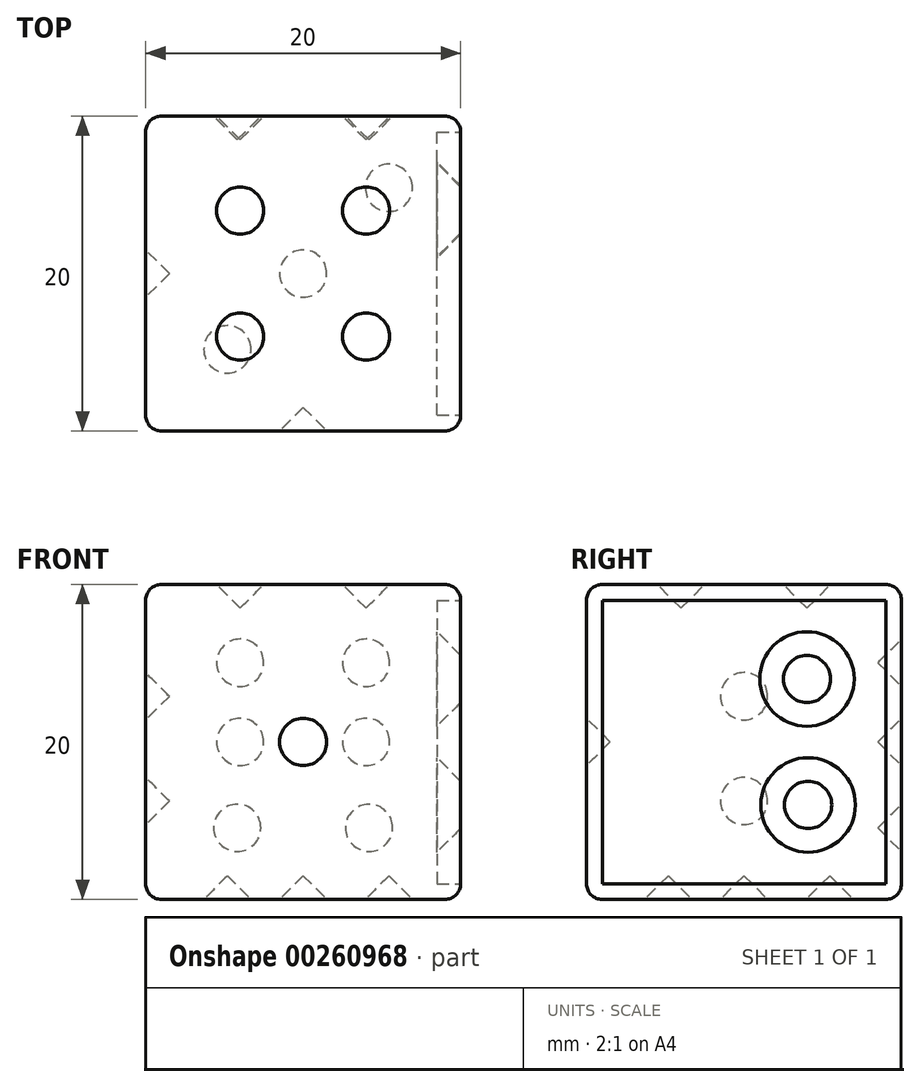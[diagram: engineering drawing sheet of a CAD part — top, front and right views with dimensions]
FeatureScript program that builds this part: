
annotation { "Feature Type Name" : "Feature", "Feature Type Description" : "" }
export const myFeature = defineFeature(function(context is Context, id is Id, definition is map)
    precondition{}
    {
        {
            var Q0;
            Q0=qCreatedBy(makeId("Top.planeOp"),FACE);
            var sketch = newSketch(context, id + "F0", { "sketchPlane" : qUnion([Q0])});
            skLineSegment(sketch, "E0.bottom", {"start": v(0, 0) * mm, "end": v(20, 0) * mm});
            skLineSegment(sketch, "E0.top", {"start": v(0, 20) * mm, "end": v(20, 20) * mm});
            skLineSegment(sketch, "E0.left", {"start": v(0, 0) * mm, "end": v(0, 20) * mm});
            skLineSegment(sketch, "E0.right", {"start": v(20, 0) * mm, "end": v(20, 20) * mm});
            skSolve(sketch);
        }
        {
            var Q0;
            Q0 = qSketchRegion(id + "F0", true);
            extrude(context, id + "F1", {"entities" : qUnion([Q0]), "depth" : 20 * mm});
        }
        {
            var Q0;
            Q0=makeQuery(id+"F1.opExtrude","SWEPT_FACE",FACE,{"disambiguationData":[OSD([sQuery(id+"F0.wireOp",EDGE,"E0.bottom")])]});
            var sketch = newSketch(context, id + "F2", { "sketchPlane" : qUnion([Q0])});
            skLineSegment(sketch, "E1.0", {"start": v(0, 20) * mm, "end": v(20, 20) * mm, "construction": true});
            skLineSegment(sketch, "E1.1", {"start": v(0, 0) * mm, "end": v(20, 0) * mm, "construction": true});
            skLineSegment(sketch, "E2", {"start": v(10, 20) * mm, "end": v(10, 0) * mm, "construction": true});
            skCircle(sketch, "E3", {"center": v(10, 10) * mm, "radius": 1.5 * mm});
            skSolve(sketch);
        }
        {
            var Q0;
            Q0 = qSketchRegion(id + "F2", true);
            extrude(context, id + "F3", {"entities" : qUnion([Q0]), "operationType" : NewBodyOperationType.REMOVE, "oppositeDirection" : true, "depth" : 1.5 * mm});
        }
        {
            var Q0;
            Q0=makeQuery(id+"F1.opExtrude","CAP_EDGE",EDGE,{"disambiguationData":[OSD([sQuery(id+"F0.wireOp",EDGE,"E0.left")])],"isStart":false});
            var Q1;
            Q1=makeQuery(id+"F1.opExtrude","CAP_EDGE",EDGE,{"disambiguationData":[OSD([sQuery(id+"F0.wireOp",EDGE,"E0.top")])],"isStart":false});
            var Q2;
            Q2=makeQuery(id+"F1.opExtrude","CAP_EDGE",EDGE,{"disambiguationData":[OSD([sQuery(id+"F0.wireOp",EDGE,"E0.right")])],"isStart":false});
            var Q3;
            Q3=makeQuery(id+"F1.opExtrude","CAP_EDGE",EDGE,{"disambiguationData":[OSD([sQuery(id+"F0.wireOp",EDGE,"E0.bottom")])],"isStart":false});
            var Q4;
            Q4=makeQuery(id+"F1.opExtrude","SWEPT_EDGE",EDGE,{"disambiguationData":[OSD([sQuery(id+"F0.wireOp",EDGE,"E0.bottom"),sQuery(id+"F0.wireOp",EDGE,"E0.right")])]});
            var Q5;
            Q5=makeQuery(id+"F1.opExtrude","CAP_EDGE",EDGE,{"disambiguationData":[OSD([sQuery(id+"F0.wireOp",EDGE,"E0.bottom")])],"isStart":true});
            var Q6;
            Q6=makeQuery(id+"F1.opExtrude","SWEPT_EDGE",EDGE,{"disambiguationData":[OSD([sQuery(id+"F0.wireOp",EDGE,"E0.bottom"),sQuery(id+"F0.wireOp",EDGE,"E0.left")])]});
            var Q7;
            Q7=makeQuery(id+"F1.opExtrude","CAP_EDGE",EDGE,{"disambiguationData":[OSD([sQuery(id+"F0.wireOp",EDGE,"E0.right")])],"isStart":true});
            var Q8;
            Q8=makeQuery(id+"F1.opExtrude","SWEPT_EDGE",EDGE,{"disambiguationData":[OSD([sQuery(id+"F0.wireOp",EDGE,"E0.top"),sQuery(id+"F0.wireOp",EDGE,"E0.right")])]});
            var Q9;
            Q9=makeQuery(id+"F1.opExtrude","CAP_EDGE",EDGE,{"disambiguationData":[OSD([sQuery(id+"F0.wireOp",EDGE,"E0.top")])],"isStart":true});
            var Q10;
            Q10=makeQuery(id+"F1.opExtrude","CAP_EDGE",EDGE,{"disambiguationData":[OSD([sQuery(id+"F0.wireOp",EDGE,"E0.left")])],"isStart":true});
            var Q11;
            Q11=makeQuery(id+"F1.opExtrude","SWEPT_EDGE",EDGE,{"disambiguationData":[OSD([sQuery(id+"F0.wireOp",EDGE,"E0.top"),sQuery(id+"F0.wireOp",EDGE,"E0.left")])]});
            fillet(context, id + "F4", {"entities" : qUnion([Q0, Q1, Q2, Q3, Q4, Q5, Q6, Q7, Q8, Q9, Q10, Q11]), "radius" : 1 * mm, "tangentPropagation" : true, "allowEdgeOverflow" : false});
        }
        {
            var Q0;
            Q0=makeQuery(id+"F1.opExtrude","CAP_FACE",FACE,{"disambiguationData":[OSD([sQuery(id+"F0.wireOp",EDGE,"E0.bottom"),sQuery(id+"F0.wireOp",EDGE,"E0.top"),sQuery(id+"F0.wireOp",EDGE,"E0.left"),sQuery(id+"F0.wireOp",EDGE,"E0.right")])],"isStart":false});
            var sketch = newSketch(context, id + "F5", { "sketchPlane" : qUnion([Q0])});
            skLineSegment(sketch, "E4.0", {"start": v(0, 0) * mm, "end": v(6, 0) * mm, "construction": true});
            skLineSegment(sketch, "E4.1", {"start": v(0, 20) * mm, "end": v(6, 20) * mm, "construction": true});
            skLineSegment(sketch, "E5", {"start": v(6, 20) * mm, "end": v(6, 14) * mm, "construction": true});
            skLineSegment(sketch, "E6", {"start": v(6, 0) * mm, "end": v(6, 6) * mm, "construction": true});
            skCircle(sketch, "E7", {"center": v(6, 14) * mm, "radius": 1.5 * mm});
            skCircle(sketch, "E8", {"center": v(6, 6) * mm, "radius": 1.5 * mm});
            skPoint(sketch, "E9.orphan", {"position": v(20, 20) * mm});
            skPoint(sketch, "E10.orphan", {"position": v(20, 0) * mm});
            skLineSegment(sketch, "E11.0", {"start": v(0, 20) * mm, "end": v(20, 20) * mm, "construction": true});
            skLineSegment(sketch, "E11.1", {"start": v(0, 0) * mm, "end": v(20, 0) * mm, "construction": true});
            skLineSegment(sketch, "E12", {"start": v(10, 20) * mm, "end": v(10, 0) * mm, "construction": true});
            skCircle(sketch, "E13.MirrorC", {"center": v(14, 6) * mm, "radius": 1.5 * mm});
            skCircle(sketch, "E14.MirrorC", {"center": v(14, 14) * mm, "radius": 1.5 * mm});
            skSolve(sketch);
        }
        {
            var Q0;
            Q0 = qSketchRegion(id + "F5", true);
            extrude(context, id + "F6", {"entities" : qUnion([Q0]), "operationType" : NewBodyOperationType.REMOVE, "oppositeDirection" : true, "depth" : 1.5 * mm});
        }
        {
            var Q0;
            Q0=makeQuery(id+"F1.opExtrude","SWEPT_FACE",FACE,{"disambiguationData":[OSD([sQuery(id+"F0.wireOp",EDGE,"E0.right")])]});
            var sketch = newSketch(context, id + "F7", { "sketchPlane" : qUnion([Q0])});
            skLineSegment(sketch, "E15.0", {"start": v(0, 20) * mm, "end": v(6, 20) * mm, "construction": true});
            skLineSegment(sketch, "E15.1", {"start": v(0, 0) * mm, "end": v(6, 0) * mm, "construction": true});
            skCircle(sketch, "E16", {"center": v(10, 10) * mm, "radius": 1.5 * mm});
            skPoint(sketch, "E17.orphan", {"position": v(20, 20) * mm});
            skPoint(sketch, "E18.orphan", {"position": v(20, 0) * mm});
            skLineSegment(sketch, "E19", {"start": v(6, 20) * mm, "end": v(6, 14) * mm, "construction": true});
            skLineSegment(sketch, "E20", {"start": v(6, 0) * mm, "end": v(5.93, 6) * mm, "construction": true});
            skCircle(sketch, "E21", {"center": v(6, 14) * mm, "radius": 1.5 * mm});
            skCircle(sketch, "E22", {"center": v(5.93, 6) * mm, "radius": 1.5 * mm});
            skLineSegment(sketch, "E23.0", {"start": v(0, 20) * mm, "end": v(20, 20) * mm, "construction": true});
            skLineSegment(sketch, "E24", {"start": v(10, 11.5) * mm, "end": v(10, 10) * mm, "construction": true});
            skPoint(sketch, "E25.orphan", {"position": v(10, 20) * mm});
            skLineSegment(sketch, "E26", {"start": v(10, 20) * mm, "end": v(10, 0) * mm, "construction": true});
            skCircle(sketch, "E27.MirrorC", {"center": v(14.07, 6) * mm, "radius": 1.5 * mm});
            skCircle(sketch, "E28.MirrorC", {"center": v(14, 14) * mm, "radius": 1.5 * mm});
            skSolve(sketch);
        }
        {
            var Q0;
            Q0=makeQuery(id+"F7.imprint","IMPRINT",FACE,{"disambiguationData":[TD([[makeQuery(id+"F7.imprint","IMPRINT",EDGE,{"derivedFrom":sQuery(id+"F7.wireOp",EDGE,"E21")}),1.0]])]});
            var Q1;
            Q1=makeQuery(id+"F7.imprint","IMPRINT",FACE,{"disambiguationData":[TD([[makeQuery(id+"F7.imprint","IMPRINT",EDGE,{"derivedFrom":sQuery(id+"F7.wireOp",EDGE,"E22")}),1.0]])]});
            var Q2;
            Q2=makeQuery(id+"F7.imprint","IMPRINT",FACE,{"disambiguationData":[TD([[makeQuery(id+"F7.imprint","IMPRINT",EDGE,{"derivedFrom":sQuery(id+"F7.wireOp",EDGE,"E16")}),1.0]])]});
            var Q3;
            Q3=makeQuery(id+"F7.imprint","IMPRINT",FACE,{"disambiguationData":[TD([[makeQuery(id+"F7.imprint","IMPRINT",EDGE,{"derivedFrom":sQuery(id+"F7.wireOp",EDGE,"E28.MirrorC")}),-1.0]])]});
            var Q4;
            Q4=makeQuery(id+"F7.imprint","IMPRINT",FACE,{"disambiguationData":[TD([[makeQuery(id+"F7.imprint","IMPRINT",EDGE,{"derivedFrom":sQuery(id+"F7.wireOp",EDGE,"E27.MirrorC")}),-1.0]])]});
            extrude(context, id + "F8", {"entities" : qUnion([Q0, Q1, Q2, Q3, Q4]), "operationType" : NewBodyOperationType.REMOVE, "oppositeDirection" : true, "depth" : 1.5 * mm});
        }
        {
            var Q0;
            Q0=makeQuery(id+"F1.opExtrude","CAP_FACE",FACE,{"disambiguationData":[OSD([sQuery(id+"F0.wireOp",EDGE,"E0.bottom"),sQuery(id+"F0.wireOp",EDGE,"E0.top"),sQuery(id+"F0.wireOp",EDGE,"E0.left"),sQuery(id+"F0.wireOp",EDGE,"E0.right")])],"isStart":true});
            var sketch = newSketch(context, id + "F9", { "sketchPlane" : qUnion([Q0])});
            skLineSegment(sketch, "E29", {"start": v(0, 0) * mm, "end": v(20, -20) * mm, "construction": true});
            skLineSegment(sketch, "E30.0", {"start": v(0, 0) * mm, "end": v(20, 0) * mm, "construction": true});
            skLineSegment(sketch, "E30.1", {"start": v(0, -20) * mm, "end": v(20, -20) * mm, "construction": true});
            skCircle(sketch, "E31", {"center": v(5.19, -5.19) * mm, "radius": 1.5 * mm});
            skCircle(sketch, "E32", {"center": v(10, -10) * mm, "radius": 1.5 * mm});
            skCircle(sketch, "E33", {"center": v(15.45, -15.45) * mm, "radius": 1.5 * mm});
            skSolve(sketch);
        }
        {
            var Q0;
            Q0 = qSketchRegion(id + "F9", true);
            extrude(context, id + "F10", {"entities" : qUnion([Q0]), "operationType" : NewBodyOperationType.REMOVE, "oppositeDirection" : true, "depth" : 1.5 * mm});
        }
        {
            var Q0;
            Q0=makeQuery(id+"F1.opExtrude","SWEPT_FACE",FACE,{"disambiguationData":[OSD([sQuery(id+"F0.wireOp",EDGE,"E0.top")])]});
            var sketch = newSketch(context, id + "F11", { "sketchPlane" : qUnion([Q0])});
            skLineSegment(sketch, "E34.0", {"start": v(-14, 20) * mm, "end": v(-20, 20) * mm, "construction": true});
            skLineSegment(sketch, "E34.1", {"start": v(-14, 0) * mm, "end": v(-20, 0) * mm, "construction": true});
            skLineSegment(sketch, "E35", {"start": v(-14, 20) * mm, "end": v(-14, 0) * mm, "construction": true});
            skPoint(sketch, "E36.orphan", {"position": v(0, 20) * mm});
            skPoint(sketch, "E37.orphan", {"position": v(0, 0) * mm});
            skCircle(sketch, "E38", {"center": v(-14, 15.03) * mm, "radius": 1.5 * mm});
            skCircle(sketch, "E39", {"center": v(-14, 10) * mm, "radius": 1.5 * mm});
            skCircle(sketch, "E40", {"center": v(-14.19, 4.54) * mm, "radius": 1.5 * mm});
            skLineSegment(sketch, "E41", {"start": v(-10, 20) * mm, "end": v(-10, 0) * mm, "construction": true});
            skCircle(sketch, "E42.MirrorC", {"center": v(-5.81, 4.54) * mm, "radius": 1.5 * mm});
            skCircle(sketch, "E43.MirrorC", {"center": v(-6, 10) * mm, "radius": 1.5 * mm});
            skCircle(sketch, "E44.MirrorC", {"center": v(-6, 15.03) * mm, "radius": 1.5 * mm});
            skSolve(sketch);
        }
        {
            var Q0;
            Q0 = qSketchRegion(id + "F11", true);
            extrude(context, id + "F12", {"entities" : qUnion([Q0]), "operationType" : NewBodyOperationType.REMOVE, "oppositeDirection" : true, "depth" : 1.5 * mm});
        }
        {
            var Q0;
            Q0=makeQuery(id+"F1.opExtrude","SWEPT_FACE",FACE,{"disambiguationData":[OSD([sQuery(id+"F0.wireOp",EDGE,"E0.left")])]});
            var sketch = newSketch(context, id + "F13", { "sketchPlane" : qUnion([Q0])});
            skLineSegment(sketch, "E45.0", {"start": v(0, 20) * mm, "end": v(-20, 20) * mm, "construction": true});
            skLineSegment(sketch, "E45.1", {"start": v(0, 0) * mm, "end": v(-20, 0) * mm, "construction": true});
            skLineSegment(sketch, "E46", {"start": v(-10, 20) * mm, "end": v(-10, 0) * mm, "construction": true});
            skCircle(sketch, "E47", {"center": v(-10, 6.25) * mm, "radius": 1.5 * mm});
            skCircle(sketch, "E48", {"center": v(-10, 12.9) * mm, "radius": 1.5 * mm});
            skSolve(sketch);
        }
        {
            var Q0;
            Q0 = qSketchRegion(id + "F13", true);
            extrude(context, id + "F14", {"entities" : qUnion([Q0]), "operationType" : NewBodyOperationType.REMOVE, "oppositeDirection" : true, "depth" : 1.5 * mm});
        }
        {
            var Q0;
            Q0=makeQuery(id+"F6.boolean.opBoolean","COPY",EDGE,{"derivedFrom":makeQuery(id+"F6.opExtrude","CAP_EDGE",EDGE,{"disambiguationData":[OSD([sQuery(id+"F5.wireOp",EDGE,"E14.MirrorC")])],"isStart":false})});
            var Q1;
            Q1=makeQuery(id+"F6.boolean.opBoolean","COPY",EDGE,{"derivedFrom":makeQuery(id+"F6.opExtrude","CAP_EDGE",EDGE,{"disambiguationData":[OSD([sQuery(id+"F5.wireOp",EDGE,"E13.MirrorC")])],"isStart":false})});
            var Q2;
            Q2=makeQuery(id+"F6.boolean.opBoolean","COPY",EDGE,{"derivedFrom":makeQuery(id+"F6.opExtrude","CAP_EDGE",EDGE,{"disambiguationData":[OSD([sQuery(id+"F5.wireOp",EDGE,"E8")])],"isStart":false})});
            var Q3;
            Q3=makeQuery(id+"F6.boolean.opBoolean","COPY",EDGE,{"derivedFrom":makeQuery(id+"F6.opExtrude","CAP_EDGE",EDGE,{"disambiguationData":[OSD([sQuery(id+"F5.wireOp",EDGE,"E7")])],"isStart":false})});
            var Q4;
            Q4=makeQuery(id+"F3.boolean.opBoolean","COPY",EDGE,{"derivedFrom":makeQuery(id+"F3.opExtrude","CAP_EDGE",EDGE,{"disambiguationData":[OSD([sQuery(id+"F2.wireOp",EDGE,"E3")])],"isStart":false})});
            var Q5;
            Q5=makeQuery(id+"F8.boolean.opBoolean","COPY",EDGE,{"derivedFrom":makeQuery(id+"F8.opExtrude","CAP_EDGE",EDGE,{"disambiguationData":[OSD([sQuery(id+"F7.wireOp",EDGE,"E16")])],"isStart":false})});
            var Q6;
            Q6=makeQuery(id+"F8.boolean.opBoolean","COPY",EDGE,{"derivedFrom":makeQuery(id+"F8.opExtrude","CAP_EDGE",EDGE,{"disambiguationData":[OSD([sQuery(id+"F7.wireOp",EDGE,"E21")])],"isStart":false})});
            var Q7;
            Q7=makeQuery(id+"F8.boolean.opBoolean","COPY",EDGE,{"derivedFrom":makeQuery(id+"F8.opExtrude","CAP_EDGE",EDGE,{"disambiguationData":[OSD([sQuery(id+"F7.wireOp",EDGE,"E28.MirrorC")])],"isStart":false})});
            var Q8;
            Q8=makeQuery(id+"F8.boolean.opBoolean","COPY",EDGE,{"derivedFrom":makeQuery(id+"F8.opExtrude","CAP_EDGE",EDGE,{"disambiguationData":[OSD([sQuery(id+"F7.wireOp",EDGE,"E27.MirrorC")])],"isStart":false})});
            var Q9;
            Q9=makeQuery(id+"F8.boolean.opBoolean","COPY",EDGE,{"derivedFrom":makeQuery(id+"F8.opExtrude","CAP_EDGE",EDGE,{"disambiguationData":[OSD([sQuery(id+"F7.wireOp",EDGE,"E22")])],"isStart":false})});
            var Q10;
            Q10=makeQuery(id+"F10.boolean.opBoolean","COPY",EDGE,{"derivedFrom":makeQuery(id+"F10.opExtrude","CAP_EDGE",EDGE,{"disambiguationData":[OSD([sQuery(id+"F9.wireOp",EDGE,"E31")])],"isStart":false})});
            var Q11;
            Q11=makeQuery(id+"F10.boolean.opBoolean","COPY",EDGE,{"derivedFrom":makeQuery(id+"F10.opExtrude","CAP_EDGE",EDGE,{"disambiguationData":[OSD([sQuery(id+"F9.wireOp",EDGE,"E32")])],"isStart":false})});
            var Q12;
            Q12=makeQuery(id+"F10.boolean.opBoolean","COPY",EDGE,{"derivedFrom":makeQuery(id+"F10.opExtrude","CAP_EDGE",EDGE,{"disambiguationData":[OSD([sQuery(id+"F9.wireOp",EDGE,"E33")])],"isStart":false})});
            var Q13;
            Q13=makeQuery(id+"F12.boolean.opBoolean","COPY",EDGE,{"derivedFrom":makeQuery(id+"F12.opExtrude","CAP_EDGE",EDGE,{"disambiguationData":[OSD([sQuery(id+"F11.wireOp",EDGE,"E38")])],"isStart":false})});
            var Q14;
            Q14=makeQuery(id+"F12.boolean.opBoolean","COPY",EDGE,{"derivedFrom":makeQuery(id+"F12.opExtrude","CAP_EDGE",EDGE,{"disambiguationData":[OSD([sQuery(id+"F11.wireOp",EDGE,"E44.MirrorC")])],"isStart":false})});
            var Q15;
            Q15=makeQuery(id+"F12.boolean.opBoolean","COPY",EDGE,{"derivedFrom":makeQuery(id+"F12.opExtrude","CAP_EDGE",EDGE,{"disambiguationData":[OSD([sQuery(id+"F11.wireOp",EDGE,"E39")])],"isStart":false})});
            var Q16;
            Q16=makeQuery(id+"F12.boolean.opBoolean","COPY",EDGE,{"derivedFrom":makeQuery(id+"F12.opExtrude","CAP_EDGE",EDGE,{"disambiguationData":[OSD([sQuery(id+"F11.wireOp",EDGE,"E43.MirrorC")])],"isStart":false})});
            var Q17;
            Q17=makeQuery(id+"F12.boolean.opBoolean","COPY",EDGE,{"derivedFrom":makeQuery(id+"F12.opExtrude","CAP_EDGE",EDGE,{"disambiguationData":[OSD([sQuery(id+"F11.wireOp",EDGE,"E40")])],"isStart":false})});
            var Q18;
            Q18=makeQuery(id+"F12.boolean.opBoolean","COPY",EDGE,{"derivedFrom":makeQuery(id+"F12.opExtrude","CAP_EDGE",EDGE,{"disambiguationData":[OSD([sQuery(id+"F11.wireOp",EDGE,"E42.MirrorC")])],"isStart":false})});
            var Q19;
            Q19=makeQuery(id+"F14.boolean.opBoolean","COPY",EDGE,{"derivedFrom":makeQuery(id+"F14.opExtrude","CAP_EDGE",EDGE,{"disambiguationData":[OSD([sQuery(id+"F13.wireOp",EDGE,"E47")])],"isStart":false})});
            var Q20;
            Q20=makeQuery(id+"F14.boolean.opBoolean","COPY",EDGE,{"derivedFrom":makeQuery(id+"F14.opExtrude","CAP_EDGE",EDGE,{"disambiguationData":[OSD([sQuery(id+"F13.wireOp",EDGE,"E48")])],"isStart":false})});
            chamfer(context, id + "F15", {"entities" : qUnion([Q0, Q1, Q2, Q3, Q4, Q5, Q6, Q7, Q8, Q9, Q10, Q11, Q12, Q13, Q14, Q15, Q16, Q17, Q18, Q19, Q20]), "width" : 1.5 * mm, "tangentPropagation" : true});
        }
    });
